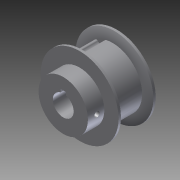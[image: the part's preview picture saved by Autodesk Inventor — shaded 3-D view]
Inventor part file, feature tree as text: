
AUTODESK INVENTOR PART (.ipt)
format: ipt  version: 2012 (Build 160160000, 160)  size: 195,072 bytes
history: native  units: in
note: dims shown in document units (in); Inventor stores cm internally (conversion verified against a paired STEP export)
features: extrude x1, imported_body x1, sketch x1
ambient origin geometry x8: Origin, YZ Plane, XZ Plane, XY Plane, X Axis, Y Axis, Z Axis, Center Point
feature tree (3):
  extrude  "Extrusion1"  Depth=0.0787in
  imported_body  "Base1"
  sketch  "Sketch2"  dims[d1=0.0787in d2=0.0787in d3=0.0394in d4=0.3157in d5=0.1972in d6=0.3937in d7=0.0in]
